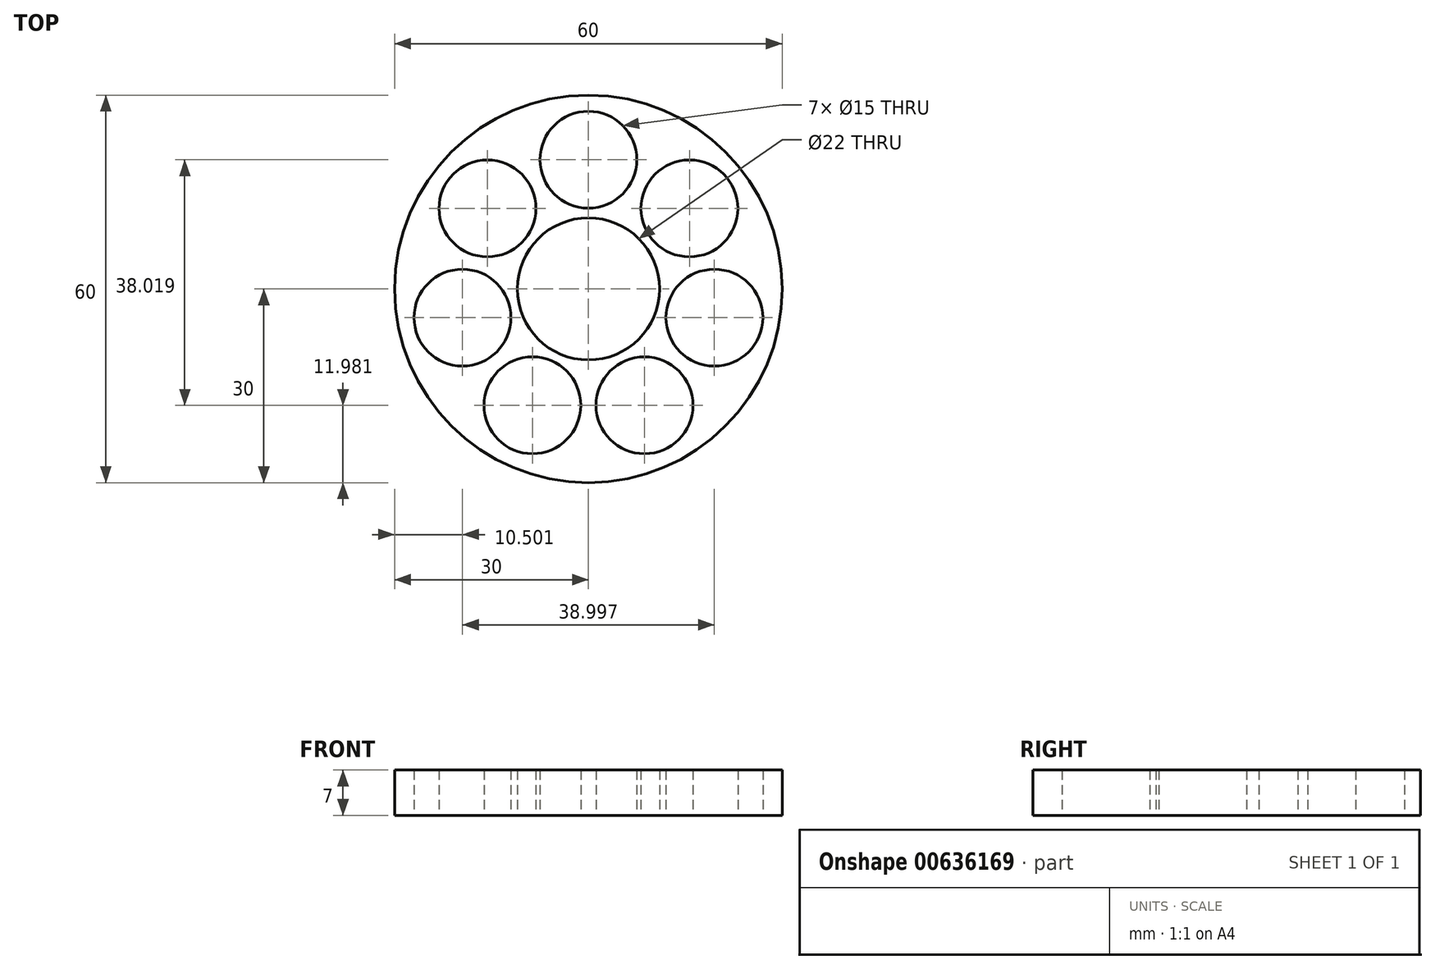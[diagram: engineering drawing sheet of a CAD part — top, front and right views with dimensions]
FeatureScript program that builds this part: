
annotation { "Feature Type Name" : "Feature", "Feature Type Description" : "" }
export const myFeature = defineFeature(function(context is Context, id is Id, definition is map)
    precondition{}
    {
        {
            var Q0;
            Q0=qCreatedBy(makeId("Top.planeOp"),FACE);
            var sketch = newSketch(context, id + "F0", { "sketchPlane" : qUnion([Q0])});
            skCircle(sketch, "E0", {"center": v(0, 0) * mm, "radius": 11 * mm});
            skCircle(sketch, "E1", {"center": v(0, 20) * mm, "radius": 7.5 * mm});
            skCircle(sketch, "E2.1.0", {"center": v(-15.64, 12.47) * mm, "radius": 7.5 * mm});
            skCircle(sketch, "E2.2.0", {"center": v(-19.5, -4.45) * mm, "radius": 7.5 * mm});
            skCircle(sketch, "E2.3.0", {"center": v(-8.68, -18.02) * mm, "radius": 7.5 * mm});
            skCircle(sketch, "E2.4.0", {"center": v(8.68, -18.02) * mm, "radius": 7.5 * mm});
            skCircle(sketch, "E2.5.0", {"center": v(19.5, -4.45) * mm, "radius": 7.5 * mm});
            skCircle(sketch, "E2.6.0", {"center": v(15.64, 12.47) * mm, "radius": 7.5 * mm});
            skCircle(sketch, "E3", {"center": v(0, 0) * mm, "radius": 30 * mm});
            skSolve(sketch);
        }
        {
            var Q0;
            Q0=makeQuery(id+"F0.imprint","IMPRINT",FACE,{"disambiguationData":[TD([[makeQuery(id+"F0.imprint","IMPRINT",EDGE,{"derivedFrom":sQuery(id+"F0.wireOp",EDGE,"E0")}),-1.0]])]});
            extrude(context, id + "F1", {"entities" : qUnion([Q0]), "depth" : 7 * mm, "offsetDistance" : 25 * mm});
        }
    });
